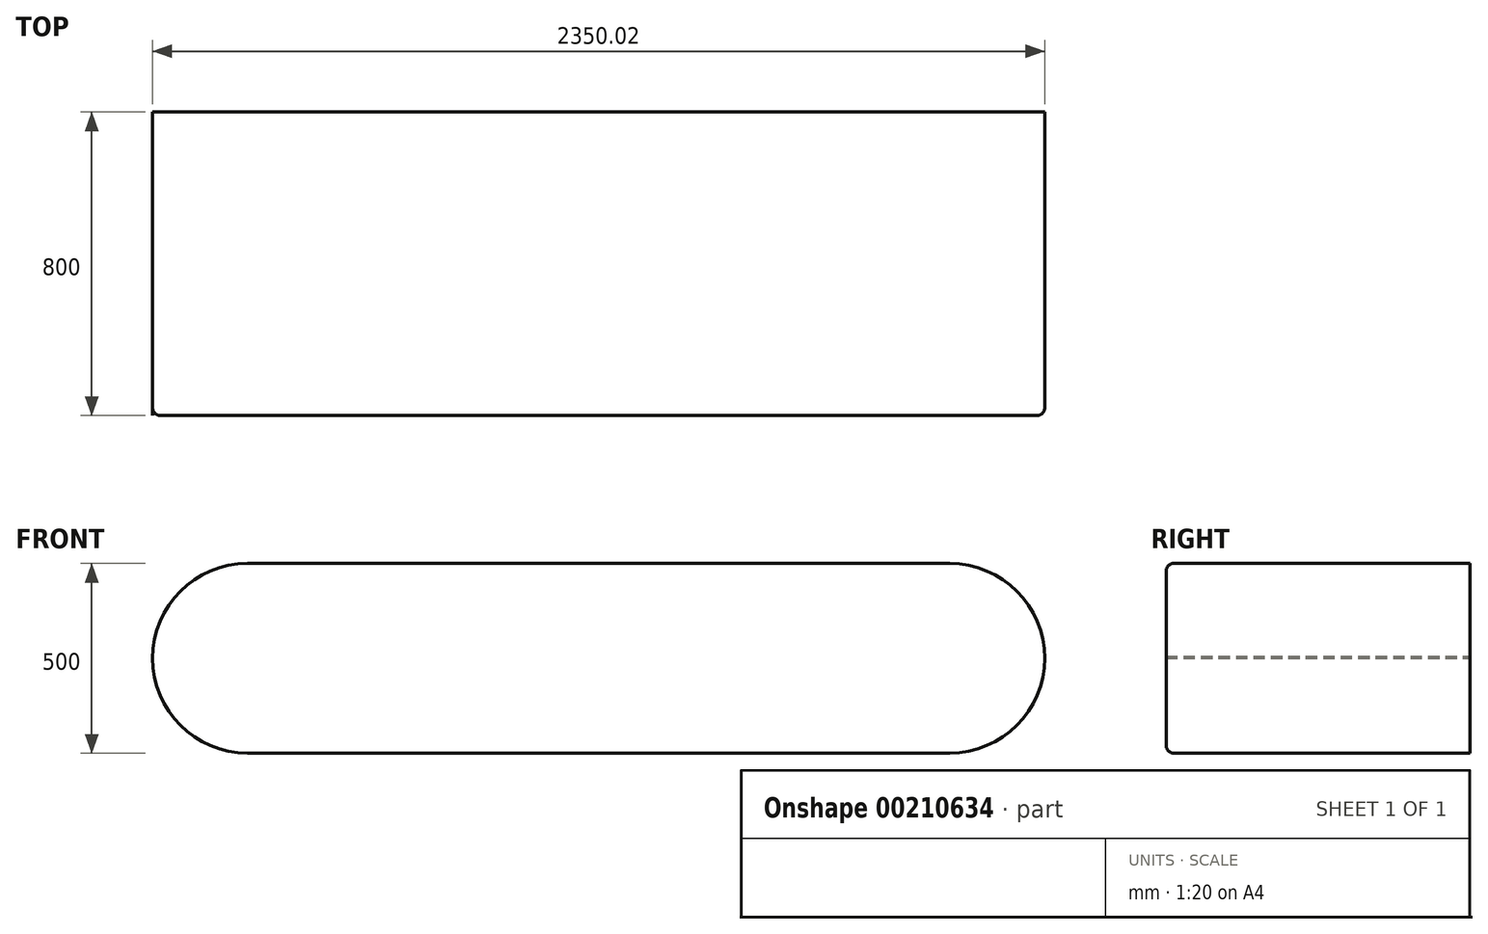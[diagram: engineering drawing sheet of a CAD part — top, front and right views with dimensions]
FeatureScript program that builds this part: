
annotation { "Feature Type Name" : "Feature", "Feature Type Description" : "" }
export const myFeature = defineFeature(function(context is Context, id is Id, definition is map)
    precondition{}
    {
        {
            var Q0;
            Q0=qCreatedBy(makeId("Front.planeOp"),FACE);
            var sketch = newSketch(context, id + "F0", { "sketchPlane" : qUnion([Q0])});
            skLineSegment(sketch, "E0.bottom", {"start": v(-250, 0) * mm, "end": v(-2100, 0) * mm});
            skLineSegment(sketch, "E0.top", {"start": v(-250, 500) * mm, "end": v(-2100, 500) * mm});
            skLineSegment(sketch, "E0.right", {"start": v(-2350, 250) * mm, "end": v(-2350, 255.76) * mm});
            skLineSegment(sketch, "E1", {"start": v(-2520.55, 250) * mm, "end": v(167, 250) * mm, "construction": true});
            skPoint(sketch, "E1.startSnap0", {"position": v(-2350, 250) * mm});
            skLineSegment(sketch, "E2", {"start": v(-2100, 645.65) * mm, "end": v(-2100, -134.84) * mm, "construction": true});
            skArc(sketch, "E3", {"start": v(-2350, 250) * mm, "mid": v(-2350.02, 252.88) * mm, "end": v(-2350, 255.76) * mm});
            skPoint(sketch, "E4.orphan", {"position": v(-2350, 500) * mm});
            skPoint(sketch, "E5.orphan", {"position": v(-2350, 0) * mm});
            skArc(sketch, "E6.trimOffspring", {"start": v(-2350, 255.76) * mm, "mid": v(-2350.02, 252.88) * mm, "end": v(-2350, 250) * mm});
            skArc(sketch, "E7", {"start": v(-2100, 0) * mm, "mid": v(-2350, 250) * mm, "end": v(-2100, 500) * mm});
            skLineSegment(sketch, "E8", {"start": v(-250, 608.76) * mm, "end": v(-250, -180.68) * mm, "construction": true});
            skArc(sketch, "E9", {"start": v(-250, 0) * mm, "mid": v(0, 250) * mm, "end": v(-250, 500) * mm});
            skSolve(sketch);
        }
        {
            var Q0;
            Q0 = qSketchRegion(id + "F0", true);
            extrude(context, id + "F1", {"entities" : qUnion([Q0]), "depth" : 800 * mm, "offsetDistance" : 25 * mm});
        }
        {
            var Q0;
            Q0=makeQuery(id+"F1.opExtrude","CAP_EDGE",EDGE,{"disambiguationData":[OSD([sQuery(id+"F0.wireOp",EDGE,"E0.bottom")])],"isStart":false});
            var Q1;
            Q1=makeQuery(id+"F1.opExtrude","CAP_EDGE",EDGE,{"disambiguationData":[OSD([sQuery(id+"F0.wireOp",EDGE,"E9")])],"isStart":false});
            var Q2;
            Q2=makeQuery(id+"F1.opExtrude","CAP_EDGE",EDGE,{"disambiguationData":[OSD([sQuery(id+"F0.wireOp",EDGE,"E7")])],"isStart":false});
            var Q3;
            Q3=makeQuery(id+"F1.opExtrude","CAP_EDGE",EDGE,{"disambiguationData":[OSD([sQuery(id+"F0.wireOp",EDGE,"E0.top")])],"isStart":false});
            fillet(context, id + "F2", {"entities" : qUnion([Q0, Q1, Q2, Q3]), "radius" : 20 * mm, "tangentPropagation" : true, "allowEdgeOverflow" : false});
        }
    });
